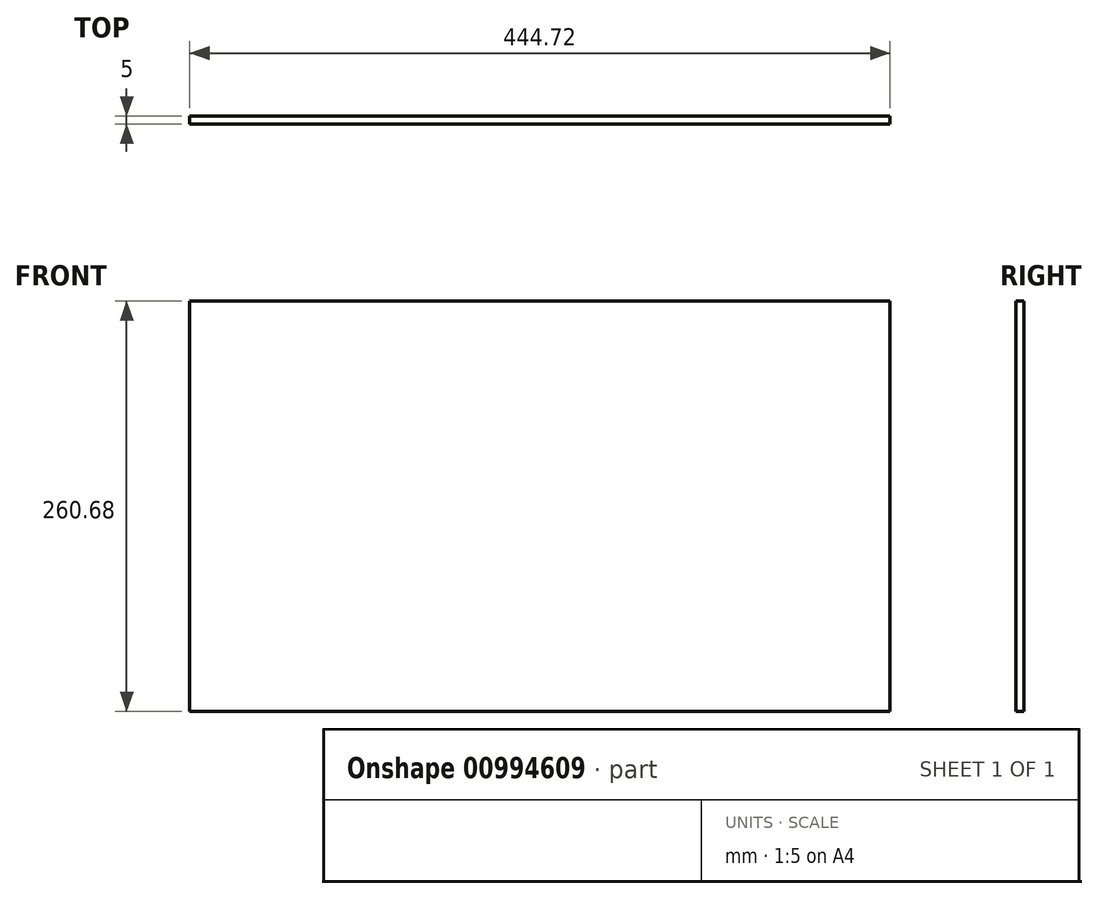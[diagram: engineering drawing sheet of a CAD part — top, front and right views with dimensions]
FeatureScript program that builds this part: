
annotation { "Feature Type Name" : "Feature", "Feature Type Description" : "" }
export const myFeature = defineFeature(function(context is Context, id is Id, definition is map)
    precondition{}
    {
        {
            var Q0;
            Q0=qCreatedBy(makeId("Front.planeOp"),FACE);
            var sketch = newSketch(context, id + "F0", { "sketchPlane" : qUnion([Q0])});
            skLineSegment(sketch, "E0.bottom", {"start": v(-222.36, -130.34) * mm, "end": v(222.36, -130.34) * mm});
            skLineSegment(sketch, "E0.top", {"start": v(-222.36, 130.34) * mm, "end": v(222.36, 130.34) * mm});
            skLineSegment(sketch, "E0.left", {"start": v(-222.36, -130.34) * mm, "end": v(-222.36, 130.34) * mm});
            skLineSegment(sketch, "E0.right", {"start": v(222.36, -130.34) * mm, "end": v(222.36, 130.34) * mm});
            skPoint(sketch, "E0.middle", {"position": v(0, 0) * mm});
            skSolve(sketch);
        }
        {
            var Q0;
            Q0=makeQuery(id+"F0.imprint","IMPRINT",FACE,{"disambiguationData":[TD([[makeQuery(id+"F0.imprint","IMPRINT",EDGE,{"derivedFrom":sQuery(id+"F0.wireOp",EDGE,"E0.bottom")}),1.0]])]});
            extrude(context, id + "F1", {"entities" : qUnion([Q0]), "depth" : 5 * mm, "offsetDistance" : 25 * mm});
        }
    });
